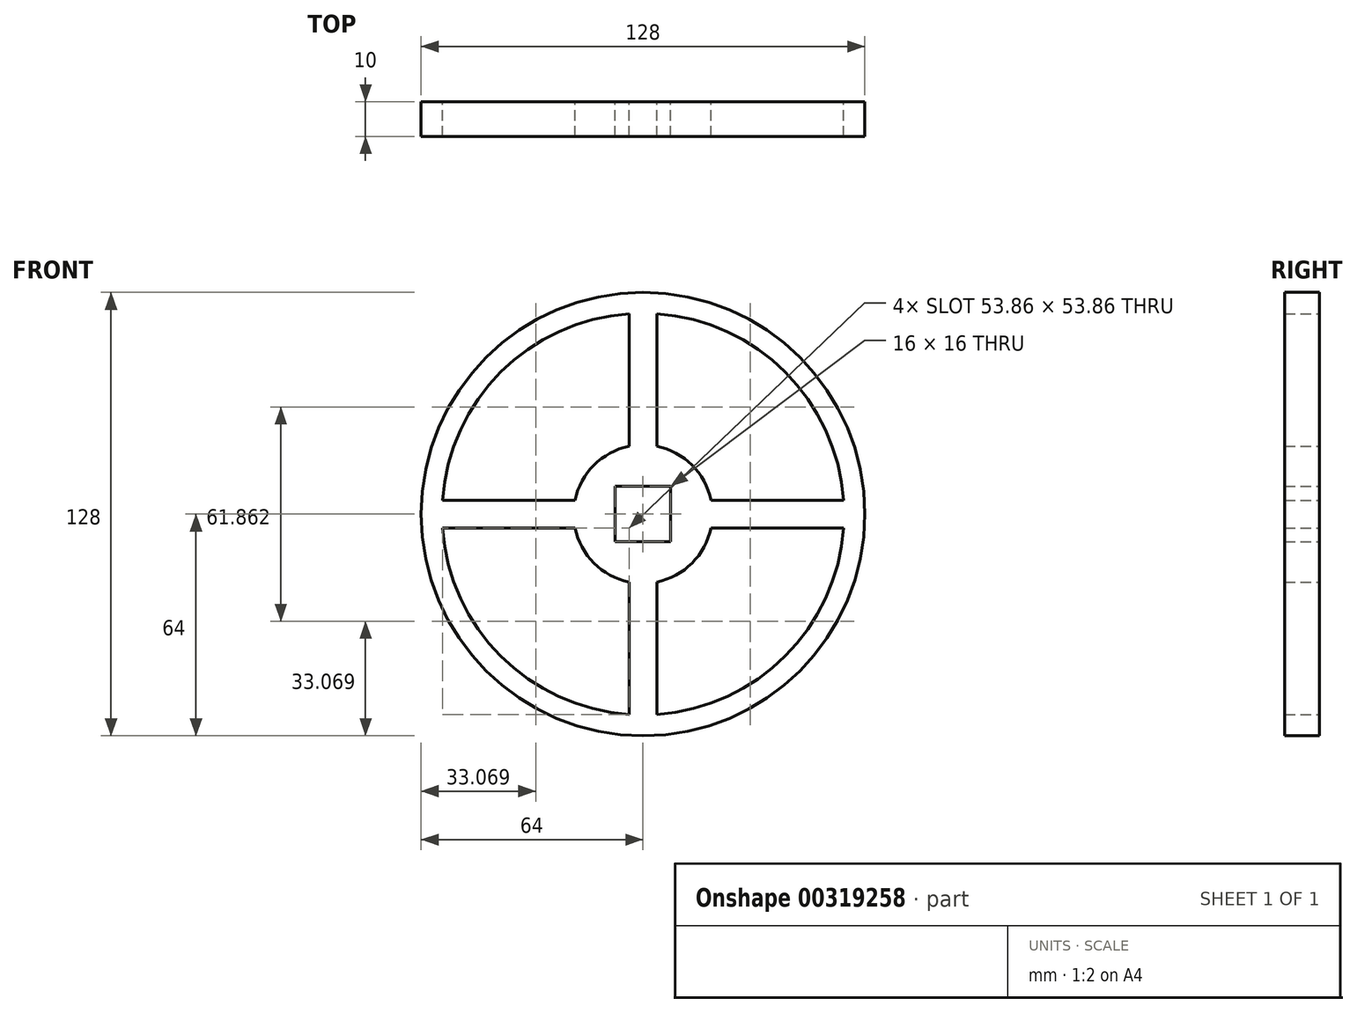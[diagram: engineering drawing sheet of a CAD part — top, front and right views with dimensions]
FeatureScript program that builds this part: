
annotation { "Feature Type Name" : "Feature", "Feature Type Description" : "" }
export const myFeature = defineFeature(function(context is Context, id is Id, definition is map)
    precondition{}
    {
        {
            var Q0;
            Q0=qCreatedBy(makeId("Front.planeOp"),FACE);
            var sketch = newSketch(context, id + "F0", { "sketchPlane" : qUnion([Q0])});
            skCircle(sketch, "E0", {"center": v(0, 0) * mm, "radius": 64 * mm});
            skArc(sketch, "E1", {"start": v(-4, 57.86) * mm, "mid": v(-41.01, 41.01) * mm, "end": v(-57.86, 4) * mm});
            skArc(sketch, "E2", {"start": v(-4, 19.6) * mm, "mid": v(-14.14, 14.14) * mm, "end": v(-19.6, 4) * mm});
            skLineSegment(sketch, "E3.left", {"start": v(-4, 57.86) * mm, "end": v(-4, 19.6) * mm});
            skLineSegment(sketch, "E3.right", {"start": v(4, 57.86) * mm, "end": v(4, 19.6) * mm});
            skLineSegment(sketch, "E4.bottom", {"start": v(57.86, 4) * mm, "end": v(19.6, 4) * mm});
            skLineSegment(sketch, "E4.top", {"start": v(57.86, -4) * mm, "end": v(19.6, -4) * mm});
            skLineSegment(sketch, "E5.trimOffspring", {"start": v(-4, -19.6) * mm, "end": v(-4, -57.86) * mm});
            skLineSegment(sketch, "E6.trimOffspring", {"start": v(-19.6, 4) * mm, "end": v(-57.86, 4) * mm});
            skLineSegment(sketch, "E7.trimOffspring", {"start": v(-19.6, -4) * mm, "end": v(-57.86, -4) * mm});
            skLineSegment(sketch, "E8.trimOffspring", {"start": v(4, -19.6) * mm, "end": v(4, -57.86) * mm});
            skArc(sketch, "E9.trimOffspring", {"start": v(-19.6, -4) * mm, "mid": v(-14.14, -14.14) * mm, "end": v(-4, -19.6) * mm});
            skArc(sketch, "E10.trimOffspring", {"start": v(19.6, 4) * mm, "mid": v(14.14, 14.14) * mm, "end": v(4, 19.6) * mm});
            skArc(sketch, "E11.trimOffspring", {"start": v(4, -19.6) * mm, "mid": v(14.14, -14.14) * mm, "end": v(19.6, -4) * mm});
            skArc(sketch, "E12.trimOffspring", {"start": v(4, -57.86) * mm, "mid": v(41.01, -41.01) * mm, "end": v(57.86, -4) * mm});
            skArc(sketch, "E13.trimOffspring", {"start": v(-57.86, -4) * mm, "mid": v(-41.01, -41.01) * mm, "end": v(-4, -57.86) * mm});
            skArc(sketch, "E14.trimOffspring", {"start": v(57.86, 4) * mm, "mid": v(41.01, 41.01) * mm, "end": v(4, 57.86) * mm});
            skLineSegment(sketch, "E15.bottom", {"start": v(-8, 8) * mm, "end": v(8, 8) * mm});
            skLineSegment(sketch, "E15.top", {"start": v(-8, -8) * mm, "end": v(8, -8) * mm});
            skLineSegment(sketch, "E15.left", {"start": v(-8, 8) * mm, "end": v(-8, -8) * mm});
            skLineSegment(sketch, "E15.right", {"start": v(8, 8) * mm, "end": v(8, -8) * mm});
            skSolve(sketch);
        }
        {
            var Q0;
            Q0=makeQuery(id+"F0.imprint","IMPRINT",FACE,{"disambiguationData":[TD([[makeQuery(id+"F0.imprint","IMPRINT",EDGE,{"derivedFrom":sQuery(id+"F0.wireOp",EDGE,"E0")}),1.0]])]});
            extrude(context, id + "F1", {"entities" : qUnion([Q0]), "depth" : 10 * mm});
        }
    });
